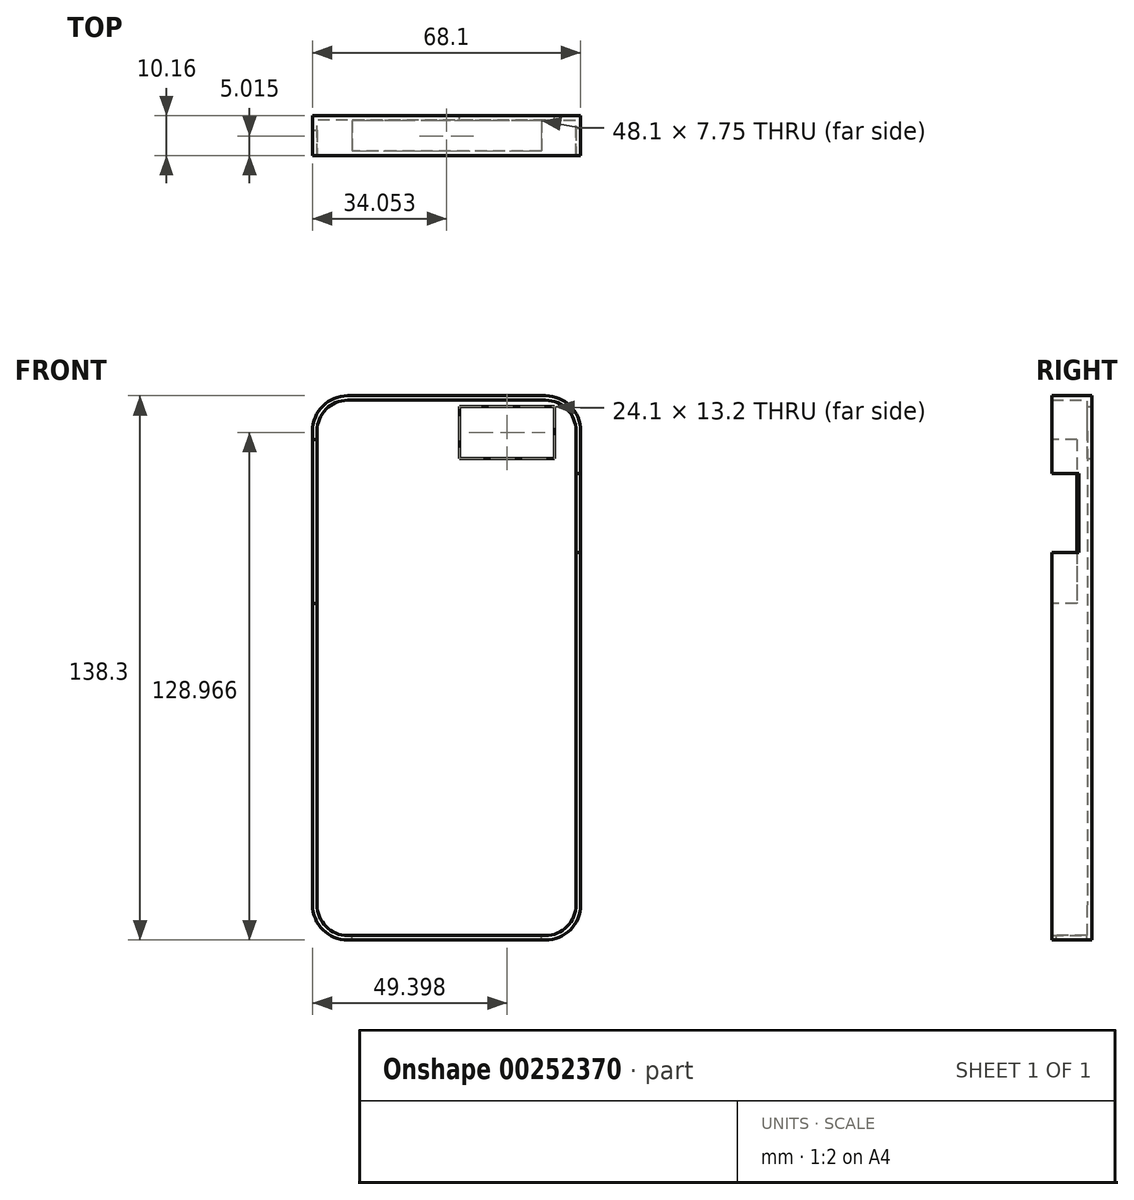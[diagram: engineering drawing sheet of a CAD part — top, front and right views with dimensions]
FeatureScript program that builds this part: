
annotation { "Feature Type Name" : "Feature", "Feature Type Description" : "" }
export const myFeature = defineFeature(function(context is Context, id is Id, definition is map)
    precondition{}
    {
        {
            var Q0;
            Q0=qCreatedBy(makeId("Front.planeOp"),FACE);
            var sketch = newSketch(context, id + "F0", { "sketchPlane" : qUnion([Q0])});
            skLineSegment(sketch, "E0.bottom", {"start": v(34.05, 69.15) * mm, "end": v(-34.05, 69.15) * mm});
            skLineSegment(sketch, "E0.top", {"start": v(34.05, -69.15) * mm, "end": v(-34.05, -69.15) * mm});
            skLineSegment(sketch, "E0.left", {"start": v(34.05, 69.15) * mm, "end": v(34.05, -69.15) * mm});
            skLineSegment(sketch, "E0.right", {"start": v(-34.05, 69.15) * mm, "end": v(-34.05, -69.15) * mm});
            skPoint(sketch, "E0.middle", {"position": v(0, 0) * mm});
            skSolve(sketch);
        }
        {
            var Q0;
            Q0=makeQuery(id+"F0.imprint","IMPRINT",FACE,{"disambiguationData":[TD([[makeQuery(id+"F0.imprint","IMPRINT",EDGE,{"derivedFrom":sQuery(id+"F0.wireOp",EDGE,"E0.bottom")}),1.0]])]});
            extrude(context, id + "F1", {"entities" : qUnion([Q0]), "endBound" : BoundingType.SYMMETRIC, "depth" : 10.16 * mm});
        }
        {
            var Q0;
            Q0=makeQuery(id+"F1.opExtrude","SWEPT_EDGE",EDGE,{"disambiguationData":[OSD([sQuery(id+"F0.wireOp",EDGE,"E0.bottom"),sQuery(id+"F0.wireOp",EDGE,"E0.right")])]});
            var Q1;
            Q1=makeQuery(id+"F1.opExtrude","SWEPT_EDGE",EDGE,{"disambiguationData":[OSD([sQuery(id+"F0.wireOp",EDGE,"E0.bottom"),sQuery(id+"F0.wireOp",EDGE,"E0.left")])]});
            var Q2;
            Q2=makeQuery(id+"F1.opExtrude","SWEPT_EDGE",EDGE,{"disambiguationData":[OSD([sQuery(id+"F0.wireOp",EDGE,"E0.top"),sQuery(id+"F0.wireOp",EDGE,"E0.left")])]});
            var Q3;
            Q3=makeQuery(id+"F1.opExtrude","SWEPT_EDGE",EDGE,{"disambiguationData":[OSD([sQuery(id+"F0.wireOp",EDGE,"E0.top"),sQuery(id+"F0.wireOp",EDGE,"E0.right")])]});
            fillet(context, id + "F2", {"entities" : qUnion([Q0, Q1, Q2, Q3]), "radius" : 8.93 * mm, "tangentPropagation" : true, "allowEdgeOverflow" : false});
        }
        {
            var Q0;
            Q0=makeQuery(id+"F1.opExtrude","CAP_FACE",FACE,{"disambiguationData":[OSD([sQuery(id+"F0.wireOp",EDGE,"E0.bottom"),sQuery(id+"F0.wireOp",EDGE,"E0.top"),sQuery(id+"F0.wireOp",EDGE,"E0.left"),sQuery(id+"F0.wireOp",EDGE,"E0.right")])],"isStart":false});
            shell(context, id + "F3", {"entities" : qUnion([Q0]), "thickness" : 1.15 * mm});
        }
        {
            var Q0;
            Q0=makeQuery(id+"F0.imprint","IMPRINT",FACE,{"disambiguationData":[TD([[makeQuery(id+"F0.imprint","IMPRINT",EDGE,{"derivedFrom":sQuery(id+"F0.wireOp",EDGE,"E0.bottom")}),1.0]])]});
            var sketch = newSketch(context, id + "F4", { "sketchPlane" : qUnion([Q0])});
            skLineSegment(sketch, "E1.bottom", {"start": v(27.4, 66.41) * mm, "end": v(3.3, 66.41) * mm});
            skLineSegment(sketch, "E1.top", {"start": v(27.4, 53.22) * mm, "end": v(3.3, 53.22) * mm});
            skLineSegment(sketch, "E1.left", {"start": v(27.4, 66.41) * mm, "end": v(27.4, 53.22) * mm});
            skLineSegment(sketch, "E1.right", {"start": v(3.3, 66.41) * mm, "end": v(3.3, 53.22) * mm});
            skSolve(sketch);
        }
        {
            var Q0;
            Q0 = qSketchRegion(id + "F4", true);
            extrude(context, id + "F5", {"entities" : qUnion([Q0]), "operationType" : NewBodyOperationType.REMOVE, "endBound" : BoundingType.SYMMETRIC, "depth" : 25 * mm});
        }
        {
            var Q0;
            Q0=makeQuery(id+"F1.opExtrude","SWEPT_FACE",FACE,{"disambiguationData":[OSD([sQuery(id+"F0.wireOp",EDGE,"E0.top")])]});
            var sketch = newSketch(context, id + "F6", { "sketchPlane" : qUnion([Q0])});
            skLineSegment(sketch, "E2.bottom", {"start": v(-24.05, 3.94) * mm, "end": v(24.05, 3.94) * mm});
            skLineSegment(sketch, "E2.top", {"start": v(-24.05, -3.81) * mm, "end": v(24.05, -3.81) * mm});
            skLineSegment(sketch, "E2.left", {"start": v(-24.05, 3.94) * mm, "end": v(-24.05, -3.81) * mm});
            skLineSegment(sketch, "E2.right", {"start": v(24.05, 3.94) * mm, "end": v(24.05, -3.81) * mm});
            skSolve(sketch);
        }
        {
            var Q0;
            {var subQ0=sQuery(id+"F6.wireOp",EDGE,"E2.bottom");Q0=makeQuery(id+"F6.imprint","IMPRINT",FACE,{"disambiguationData":[TD([[makeQuery(id+"F6.imprint","IMPRINT",EDGE,{"derivedFrom":subQ0}),-1.0]])]});}
            var Q1;
            {var subQ0=sQuery(id+"F6.wireOp",EDGE,"E2.top");Q1=makeQuery(id+"F6.imprint","IMPRINT",FACE,{"disambiguationData":[TD([[makeQuery(id+"F6.imprint","IMPRINT",EDGE,{"derivedFrom":subQ0}),1.0]])]});}
            extrude(context, id + "F7", {"entities" : qUnion([Q0, Q1]), "operationType" : NewBodyOperationType.REMOVE, "endBound" : BoundingType.SYMMETRIC, "depth" : 25 * mm});
        }
        {
            var Q0;
            Q0=makeQuery(id+"F1.opExtrude","SWEPT_FACE",FACE,{"disambiguationData":[OSD([sQuery(id+"F0.wireOp",EDGE,"E0.right")])]});
            var sketch = newSketch(context, id + "F8", { "sketchPlane" : qUnion([Q0])});
            skLineSegment(sketch, "E3.bottom", {"start": v(-1.38, 58.06) * mm, "end": v(8.73, 58.06) * mm});
            skLineSegment(sketch, "E3.top", {"start": v(-1.38, 16.4) * mm, "end": v(8.73, 16.4) * mm});
            skLineSegment(sketch, "E3.left", {"start": v(-1.38, 58.06) * mm, "end": v(-1.38, 16.4) * mm});
            skLineSegment(sketch, "E3.right", {"start": v(8.73, 58.06) * mm, "end": v(8.73, 16.4) * mm});
            skSolve(sketch);
        }
        {
            var Q0;
            Q0 = qSketchRegion(id + "F8", true);
            extrude(context, id + "F9", {"entities" : qUnion([Q0]), "operationType" : NewBodyOperationType.REMOVE, "endBound" : BoundingType.SYMMETRIC, "depth" : 25 * mm});
        }
        {
            var Q0;
            Q0=makeQuery(id+"F1.opExtrude","SWEPT_FACE",FACE,{"disambiguationData":[OSD([sQuery(id+"F0.wireOp",EDGE,"E0.left")])]});
            var sketch = newSketch(context, id + "F10", { "sketchPlane" : qUnion([Q0])});
            skLineSegment(sketch, "E4.bottom", {"start": v(-5.08, 49.35) * mm, "end": v(1.78, 49.35) * mm});
            skLineSegment(sketch, "E4.top", {"start": v(-5.08, 29.37) * mm, "end": v(1.78, 29.37) * mm});
            skLineSegment(sketch, "E4.left", {"start": v(-5.08, 49.35) * mm, "end": v(-5.08, 29.37) * mm});
            skLineSegment(sketch, "E4.right", {"start": v(1.78, 49.35) * mm, "end": v(1.78, 29.37) * mm});
            skSolve(sketch);
        }
        {
            var Q0;
            Q0=makeQuery(id+"F10.imprint","IMPRINT",FACE,{"disambiguationData":[TD([[makeQuery(id+"F10.imprint","IMPRINT",EDGE,{"derivedFrom":sQuery(id+"F10.wireOp",EDGE,"E4.bottom")}),-1.0]])]});
            extrude(context, id + "F11", {"entities" : qUnion([Q0]), "operationType" : NewBodyOperationType.REMOVE, "endBound" : BoundingType.SYMMETRIC, "depth" : 25 * mm});
        }
    });
